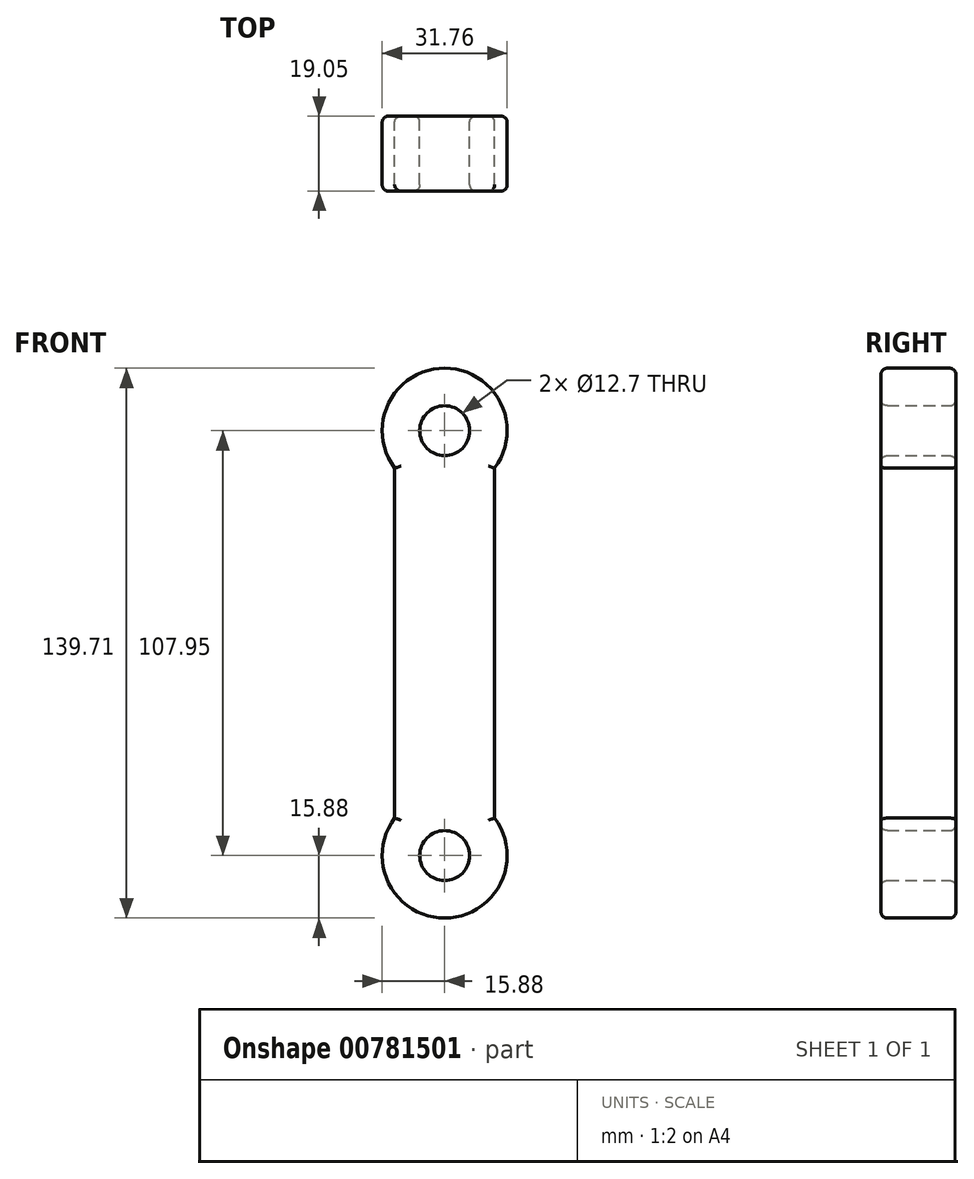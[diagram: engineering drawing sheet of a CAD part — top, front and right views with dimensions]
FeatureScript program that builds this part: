
annotation { "Feature Type Name" : "Feature", "Feature Type Description" : "" }
export const myFeature = defineFeature(function(context is Context, id is Id, definition is map)
    precondition{}
    {
        {
            var Q0;
            Q0=qCreatedBy(makeId("Front.planeOp"),FACE);
            var sketch = newSketch(context, id + "F0", { "sketchPlane" : qUnion([Q0])});
            skArc(sketch, "E0", {"start": v(-12.7, 9.52) * mm, "mid": v(0, -15.88) * mm, "end": v(12.7, 9.52) * mm});
            skCircle(sketch, "E1", {"center": v(0, 0) * mm, "radius": 6.35 * mm});
            skLineSegment(sketch, "E2.left", {"start": v(12.7, 9.52) * mm, "end": v(12.7, 98.42) * mm});
            skLineSegment(sketch, "E2.right", {"start": v(-12.7, 9.52) * mm, "end": v(-12.7, 98.42) * mm});
            skArc(sketch, "E3", {"start": v(12.7, 98.43) * mm, "mid": v(0, 123.83) * mm, "end": v(-12.7, 98.42) * mm});
            skCircle(sketch, "E4", {"center": v(0, 107.95) * mm, "radius": 6.35 * mm});
            skSolve(sketch);
        }
        {
            var Q0;
            Q0 = qSketchRegion(id + "F0", true);
            extrude(context, id + "F1", {"entities" : qUnion([Q0]), "depth" : 19.05 * mm, "offsetDistance" : 25.4 * mm});
        }
        {
            var Q0;
            Q0=makeQuery(id+"F1.opExtrude","CAP_FACE",FACE,{"disambiguationData":[OSD([sQuery(id+"F0.wireOp",EDGE,"E0"),sQuery(id+"F0.wireOp",EDGE,"E1"),sQuery(id+"F0.wireOp",EDGE,"E2.left"),sQuery(id+"F0.wireOp",EDGE,"E2.right"),sQuery(id+"F0.wireOp",EDGE,"E3"),sQuery(id+"F0.wireOp",EDGE,"E4")])],"isStart":false});
            var Q1;
            Q1=makeQuery(id+"F1.opExtrude","CAP_FACE",FACE,{"disambiguationData":[OSD([sQuery(id+"F0.wireOp",EDGE,"E0"),sQuery(id+"F0.wireOp",EDGE,"E1"),sQuery(id+"F0.wireOp",EDGE,"E2.left"),sQuery(id+"F0.wireOp",EDGE,"E2.right"),sQuery(id+"F0.wireOp",EDGE,"E3"),sQuery(id+"F0.wireOp",EDGE,"E4")])],"isStart":true});
            fillet(context, id + "F2", {"entities" : qUnion([Q0, Q1]), "radius" : 1.59 * mm, "tangentPropagation" : true, "allowEdgeOverflow" : false});
        }
    });
